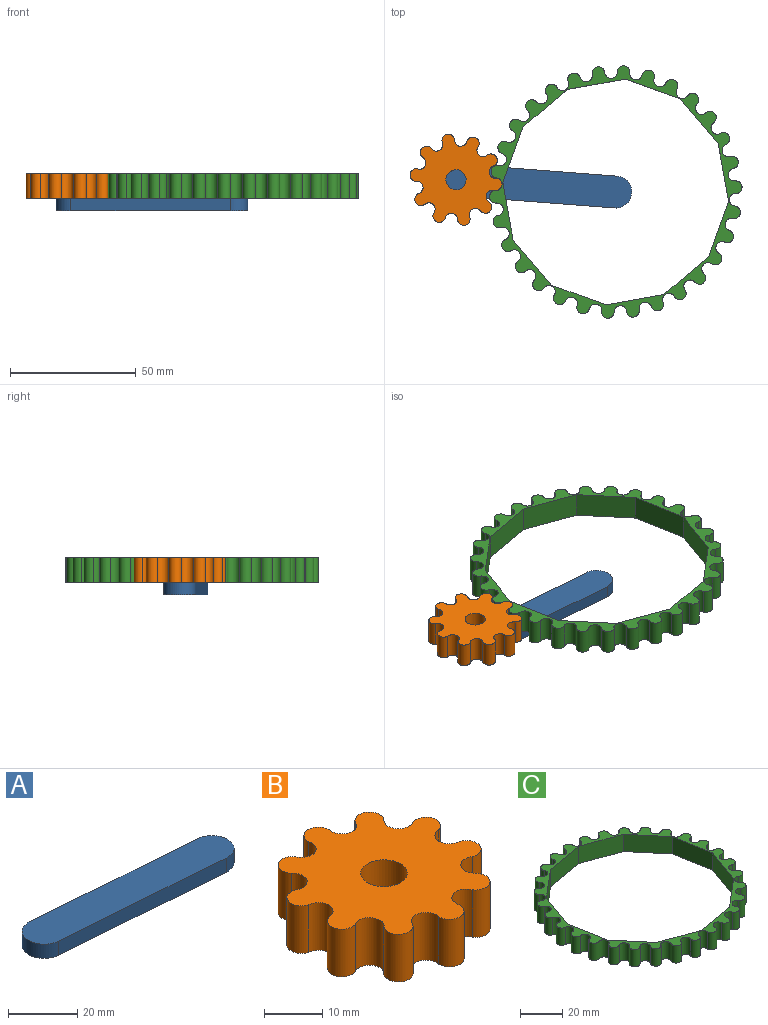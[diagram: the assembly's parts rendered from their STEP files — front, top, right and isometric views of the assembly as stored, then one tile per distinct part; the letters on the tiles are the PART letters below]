
ASSEMBLY  parts=3 mates=2
PART A: 6 faces, bbox 76.2x17.6x5 mm
  f0: plane 63.47x5mm, normal (0.08,1,0), area 318.3mm2, adj f1,f3,f4,f5
  f1: cylinder r=6.35mm len=12.68mm, axis (0,0,-1), area 99.7mm2, adj f0,f2,f4,f5
  f2: plane 63.47x5mm, normal (-0.08,-1,0), area 318.3mm2, adj f1,f3,f4,f5
  f3: cylinder r=6.35mm len=12.68mm, axis (0,0,-1), area 99.7mm2, adj f0,f2,f4,f5
  f4: plane 76.17x17.56mm, normal (0,0,1), area 935.2mm2, adj f0,f1,f2,f3
  f5: plane 76.17x17.56mm, normal (0,0,-1), area 935.2mm2, adj f0,f1,f2,f3
PART B: 23 faces, bbox 35.3x36.8x10 mm
  f0: cylinder r=2.5mm len=10mm, axis (0,0,-1), area 75.2mm2, adj f1,f20,f21,f22
  f1: cylinder r=2.5mm len=10mm, axis (0,0,-1), area 81.8mm2, adj f0,f2,f21,f22
  f2: cylinder r=2.5mm len=10mm, axis (0,0,-1), area 75.2mm2, adj f1,f3,f21,f22
  f3: cylinder r=2.5mm len=10mm, axis (0,0,-1), area 81.8mm2, adj f2,f4,f21,f22
  f4: cylinder r=2.5mm len=10mm, axis (0,0,-1), area 75.2mm2, adj f3,f5,f21,f22
  f5: cylinder r=2.5mm len=10mm, axis (0,0,-1), area 81.8mm2, adj f4,f6,f21,f22
  f6: cylinder r=2.5mm len=10mm, axis (0,0,-1), area 75.2mm2, adj f5,f7,f21,f22
  f7: cylinder r=2.5mm len=10mm, axis (0,0,-1), area 81.8mm2, adj f6,f8,f21,f22
  f8: cylinder r=2.5mm len=10mm, axis (0,0,-1), area 75.2mm2, adj f7,f9,f21,f22
  f9: cylinder r=2.5mm len=10mm, axis (0,0,-1), area 81.8mm2, adj f8,f10,f21,f22
  f10: cylinder r=2.5mm len=10mm, axis (0,0,-1), area 75.2mm2, adj f9,f11,f21,f22
  f11: cylinder r=2.5mm len=10mm, axis (0,0,-1), area 81.8mm2, adj f10,f12,f21,f22
  f12: cylinder r=2.5mm len=10mm, axis (0,0,-1), area 75.2mm2, adj f11,f13,f21,f22
  f13: cylinder r=2.5mm len=10mm, axis (0,0,-1), area 81.8mm2, adj f12,f14,f21,f22
  f14: cylinder r=2.5mm len=10mm, axis (0,0,-1), area 75.2mm2, adj f13,f15,f21,f22
  f15: cylinder r=2.5mm len=10mm, axis (0,0,-1), area 81.8mm2, adj f14,f16,f21,f22
  f16: cylinder r=2.5mm len=10mm, axis (0,0,-1), area 75.2mm2, adj f15,f17,f21,f22
  f17: cylinder r=2.5mm len=10mm, axis (0,0,-1), area 81.8mm2, adj f16,f18,f21,f22
  f18: cylinder r=2.5mm len=10mm, axis (0,0,-1), area 75.2mm2, adj f17,f20,f21,f22
  f19: cylinder r=4mm len=10mm, axis (0,0,-1), area 251.3mm2, adj f21,f22
  f20: cylinder r=2.5mm len=10mm, axis (0,0,-1), area 81.8mm2, adj f0,f18,f21,f22
  f21: plane 36.83x35.27mm, normal (0,0,1), area 752mm2, adj f0,f1,f2,f3,f4,f5,f6,f7
  f22: plane 36.83x35.27mm, normal (0,0,-1), area 752mm2, adj f0,f1,f2,f3,f4,f5,f6,f7
PART C: 74 faces, bbox 100x100.5x10 mm
  f0: plane 22.95x10mm, normal (-0.98,-0.18,0), area 233.1mm2, adj f1,f71,f72,f73
  f1: plane 21.92x10mm, normal (-0.94,0.34,0), area 233.1mm2, adj f0,f2,f72,f73
  f2: plane 17.82x15.03mm, normal (-0.64,0.76,0), area 233.1mm2, adj f1,f3,f72,f73
  f3: plane 22.95x10mm, normal (-0.18,0.98,0), area 233.1mm2, adj f2,f4,f72,f73
  f4: plane 21.92x10mm, normal (0.34,0.94,0), area 233.1mm2, adj f3,f5,f72,f73
  f5: plane 17.82x15.03mm, normal (0.76,0.64,0), area 233.1mm2, adj f4,f6,f72,f73
  f6: plane 22.95x10mm, normal (0.98,0.18,0), area 233.1mm2, adj f5,f7,f72,f73
  f7: plane 21.92x10mm, normal (0.94,-0.34,0), area 233.1mm2, adj f6,f8,f72,f73
  f8: plane 17.82x15.03mm, normal (0.64,-0.76,0), area 233.1mm2, adj f7,f9,f72,f73
  f9: plane 22.95x10mm, normal (0.18,-0.98,0), area 233.1mm2, adj f8,f10,f72,f73
  f10: plane 21.92x10mm, normal (-0.34,-0.94,0), area 233.1mm2, adj f9,f71,f72,f73
  f11: cylinder r=2.5mm len=10mm, axis (0,0,-1), area 77.5mm2, adj f12,f70,f72,f73
  f12: cylinder r=2.5mm len=10mm, axis (0,0,-1), area 79.6mm2, adj f11,f13,f72,f73
  f13: cylinder r=2.5mm len=10mm, axis (0,0,-1), area 77.5mm2, adj f12,f14,f72,f73
  f14: cylinder r=2.5mm len=10mm, axis (0,0,-1), area 79.6mm2, adj f13,f15,f72,f73
  f15: cylinder r=2.5mm len=10mm, axis (0,0,-1), area 77.5mm2, adj f14,f16,f72,f73
  f16: cylinder r=2.5mm len=10mm, axis (0,0,-1), area 79.6mm2, adj f15,f17,f72,f73
  f17: cylinder r=2.5mm len=10mm, axis (0,0,-1), area 77.5mm2, adj f16,f18,f72,f73
  f18: cylinder r=2.5mm len=10mm, axis (0,0,-1), area 79.6mm2, adj f17,f19,f72,f73
  f19: cylinder r=2.5mm len=10mm, axis (0,0,-1), area 77.5mm2, adj f18,f20,f72,f73
  f20: cylinder r=2.5mm len=10mm, axis (0,0,-1), area 79.6mm2, adj f19,f21,f72,f73
  f21: cylinder r=2.5mm len=10mm, axis (0,0,-1), area 77.5mm2, adj f20,f22,f72,f73
  f22: cylinder r=2.5mm len=10mm, axis (0,0,-1), area 79.6mm2, adj f21,f23,f72,f73
  f23: cylinder r=2.5mm len=10mm, axis (0,0,-1), area 77.5mm2, adj f22,f24,f72,f73
  f24: cylinder r=2.5mm len=10mm, axis (0,0,-1), area 79.6mm2, adj f23,f25,f72,f73
  f25: cylinder r=2.5mm len=10mm, axis (0,0,-1), area 77.5mm2, adj f24,f26,f72,f73
  f26: cylinder r=2.5mm len=10mm, axis (0,0,-1), area 79.6mm2, adj f25,f27,f72,f73
  f27: cylinder r=2.5mm len=10mm, axis (0,0,-1), area 77.5mm2, adj f26,f28,f72,f73
  f28: cylinder r=2.5mm len=10mm, axis (0,0,-1), area 79.6mm2, adj f27,f29,f72,f73
  f29: cylinder r=2.5mm len=10mm, axis (0,0,-1), area 77.5mm2, adj f28,f30,f72,f73
  f30: cylinder r=2.5mm len=10mm, axis (0,0,-1), area 79.6mm2, adj f29,f31,f72,f73
  f31: cylinder r=2.5mm len=10mm, axis (0,0,-1), area 77.5mm2, adj f30,f32,f72,f73
  f32: cylinder r=2.5mm len=10mm, axis (0,0,-1), area 79.6mm2, adj f31,f33,f72,f73
  f33: cylinder r=2.5mm len=10mm, axis (0,0,-1), area 77.5mm2, adj f32,f34,f72,f73
  f34: cylinder r=2.5mm len=10mm, axis (0,0,-1), area 79.6mm2, adj f33,f35,f72,f73
  f35: cylinder r=2.5mm len=10mm, axis (0,0,-1), area 77.5mm2, adj f34,f36,f72,f73
  f36: cylinder r=2.5mm len=10mm, axis (0,0,-1), area 79.6mm2, adj f35,f37,f72,f73
  f37: cylinder r=2.5mm len=10mm, axis (0,0,-1), area 77.5mm2, adj f36,f38,f72,f73
  f38: cylinder r=2.5mm len=10mm, axis (0,0,-1), area 79.6mm2, adj f37,f39,f72,f73
  f39: cylinder r=2.5mm len=10mm, axis (0,0,-1), area 77.5mm2, adj f38,f40,f72,f73
  f40: cylinder r=2.5mm len=10mm, axis (0,0,-1), area 79.6mm2, adj f39,f41,f72,f73
  f41: cylinder r=2.5mm len=10mm, axis (0,0,-1), area 77.5mm2, adj f40,f42,f72,f73
  f42: cylinder r=2.5mm len=10mm, axis (0,0,-1), area 79.6mm2, adj f41,f43,f72,f73
  f43: cylinder r=2.5mm len=10mm, axis (0,0,-1), area 77.5mm2, adj f42,f44,f72,f73
  f44: cylinder r=2.5mm len=10mm, axis (0,0,-1), area 79.6mm2, adj f43,f45,f72,f73
  f45: cylinder r=2.5mm len=10mm, axis (0,0,-1), area 77.5mm2, adj f44,f46,f72,f73
  f46: cylinder r=2.5mm len=10mm, axis (0,0,-1), area 79.6mm2, adj f45,f47,f72,f73
  f47: cylinder r=2.5mm len=10mm, axis (0,0,-1), area 77.5mm2, adj f46,f48,f72,f73
  f48: cylinder r=2.5mm len=10mm, axis (0,0,-1), area 79.6mm2, adj f47,f49,f72,f73
  f49: cylinder r=2.5mm len=10mm, axis (0,0,-1), area 77.5mm2, adj f48,f50,f72,f73
  f50: cylinder r=2.5mm len=10mm, axis (0,0,-1), area 79.6mm2, adj f49,f51,f72,f73
  f51: cylinder r=2.5mm len=10mm, axis (0,0,-1), area 77.5mm2, adj f50,f52,f72,f73
  f52: cylinder r=2.5mm len=10mm, axis (0,0,-1), area 79.6mm2, adj f51,f53,f72,f73
  f53: cylinder r=2.5mm len=10mm, axis (0,0,-1), area 77.5mm2, adj f52,f54,f72,f73
  f54: cylinder r=2.5mm len=10mm, axis (0,0,-1), area 79.6mm2, adj f53,f55,f72,f73
  f55: cylinder r=2.5mm len=10mm, axis (0,0,-1), area 77.5mm2, adj f54,f56,f72,f73
  f56: cylinder r=2.5mm len=10mm, axis (0,0,-1), area 79.6mm2, adj f55,f57,f72,f73
  f57: cylinder r=2.5mm len=10mm, axis (0,0,-1), area 77.5mm2, adj f56,f58,f72,f73
  f58: cylinder r=2.5mm len=10mm, axis (0,0,-1), area 79.6mm2, adj f57,f59,f72,f73
  f59: cylinder r=2.5mm len=10mm, axis (0,0,-1), area 77.5mm2, adj f58,f60,f72,f73
  f60: cylinder r=2.5mm len=10mm, axis (0,0,-1), area 79.6mm2, adj f59,f61,f72,f73
  f61: cylinder r=2.5mm len=10mm, axis (0,0,-1), area 77.5mm2, adj f60,f62,f72,f73
  f62: cylinder r=2.5mm len=10mm, axis (0,0,-1), area 79.6mm2, adj f61,f63,f72,f73
  f63: cylinder r=2.5mm len=10mm, axis (0,0,-1), area 77.5mm2, adj f62,f64,f72,f73
  f64: cylinder r=2.5mm len=10mm, axis (0,0,-1), area 79.6mm2, adj f63,f65,f72,f73
  f65: cylinder r=2.5mm len=10mm, axis (0,0,-1), area 77.5mm2, adj f64,f66,f72,f73
  f66: cylinder r=2.5mm len=10mm, axis (0,0,-1), area 79.6mm2, adj f65,f67,f72,f73
  f67: cylinder r=2.5mm len=10mm, axis (0,0,-1), area 77.5mm2, adj f66,f68,f72,f73
  f68: cylinder r=2.5mm len=10mm, axis (0,0,-1), area 79.6mm2, adj f67,f69,f72,f73
  f69: cylinder r=2.5mm len=10mm, axis (0,0,-1), area 77.5mm2, adj f68,f70,f72,f73
  f70: cylinder r=2.5mm len=10mm, axis (0,0,-1), area 79.6mm2, adj f11,f69,f72,f73
  f71: plane 17.82x15.03mm, normal (-0.76,-0.64,0), area 233.1mm2, adj f0,f10,f72,f73
  f72: plane 100.49x99.97mm, normal (0,0,1), area 1083.8mm2, adj f0,f1,f2,f3,f4,f5,f6,f7
  f73: plane 100.49x99.97mm, normal (0,0,-1), area 1083.8mm2, adj f0,f1,f2,f3,f4,f5,f6,f7
PLACE A t=(10.26,-3.08,0)mm fixed
PLACE B rot(axis=(0.51,0.86,0),180deg) t=(-74.76,-156.6,15)mm
PLACE C rot(axis=(-0.94,0.34,0),180deg) t=(56.74,-106.77,15)mm
MATE revolute B.f19 <-> A.f1  axis (0,0,-1) through (-56.72,-90.46,5)mm
MATE revolute C.f72 <-> A.f3  axis (0,0,-1) through (6.75,-95.32,5)mm
